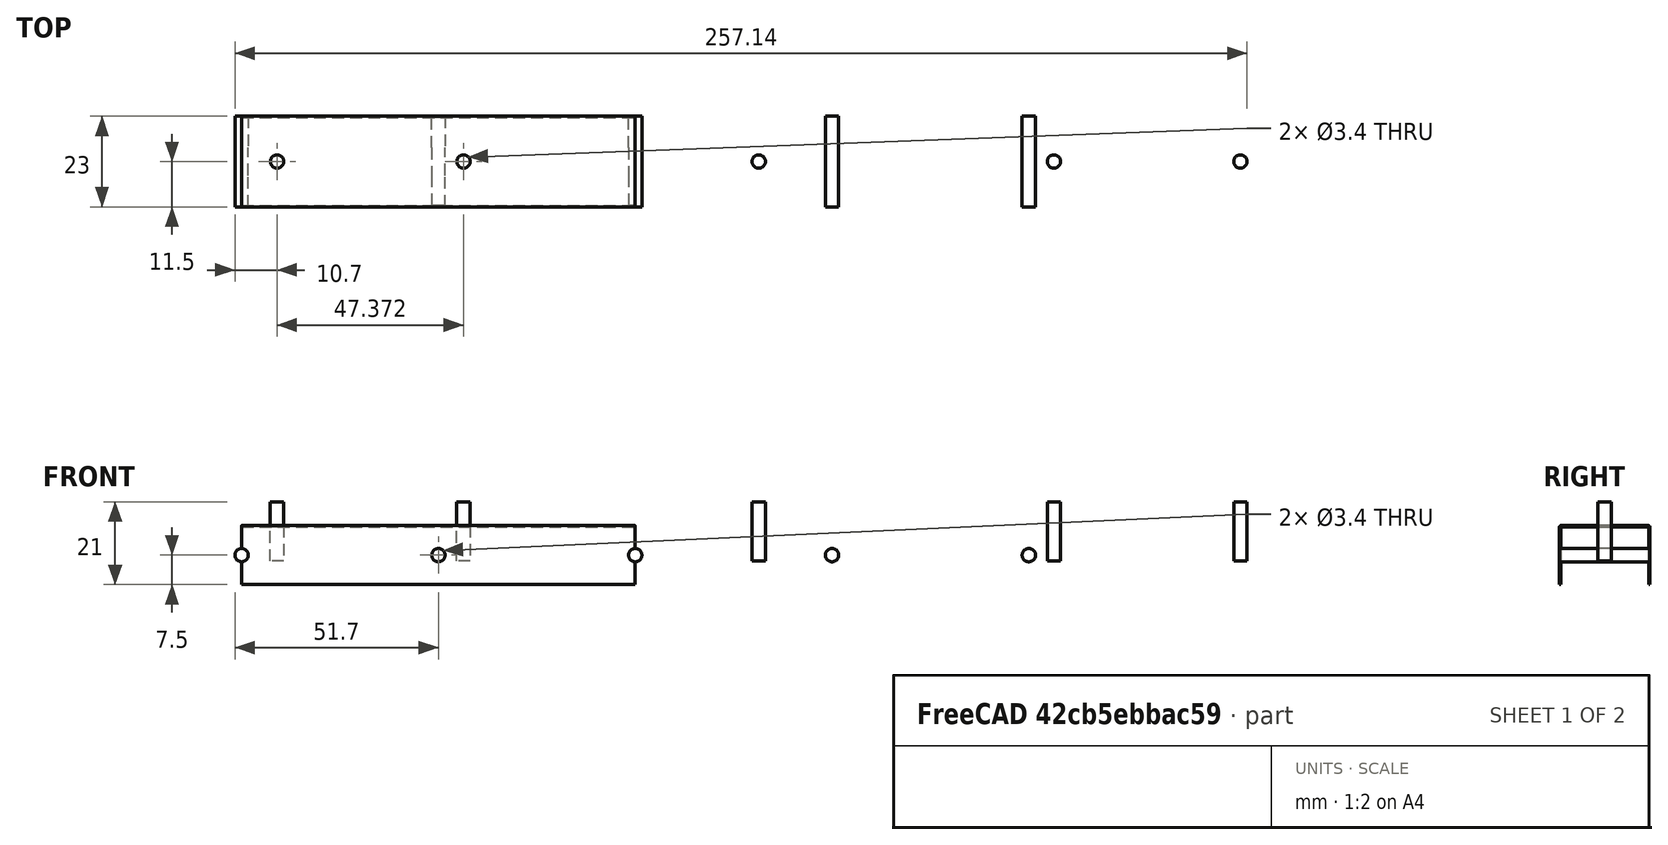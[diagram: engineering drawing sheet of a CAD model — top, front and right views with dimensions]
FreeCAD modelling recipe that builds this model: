
FCSTD DOCUMENT  (FreeCAD 1.1R38827 (Git))
Label: composit_stand3_dropper_fix_fixture_model
License: All rights reserved
LicenseURL: http://en.wikipedia.org/wiki/All_rights_reserved
objects: App::Link×4, Part::FeaturePython×3, PartDesign::SubShapeBinder×2, PartDesign::Body×2, PartDesign::FeaturePython×1, Part::MultiFuse×1, PartDesign::Boolean×1, PartDesign::CoordinateSystem×1
note: 13 computed .brp shape members not serialized (recipe doc carries the construction recipe); baked Part::Feature solids carry a one-line shape summary decoded from their .brp
EXTERNAL_REF file=composit_stand3_dropper_fix_fixture_main.FCStd obj=Sketch
EXTERNAL_REF file=composit_stand3_dropper_fix_fixture_main.FCStd obj=Placment
EXTERNAL_REF file=composit_stand3_main.FCStd obj=Cylinder
EXTERNAL_REF file=composit_stand3_dropper_fix_fixture_main.FCStd obj=Join
EXTERNAL_REF file=composit_stand3_dropper_fix_main.FCStd obj=Join

FEATURE [PartDesign::SubShapeBinder] Binder
  BindCopyOnChange = 0
  BindMode = 0
  ClaimChildren = true
  Fuse = false
  MakeFace = true
  OffsetFill = false
  OffsetIntersection = false
  OffsetJoinType = 0
  OffsetOpenResult = false
  PartialLoad = false
  Placement = pos=(0,0,0) rot=(0.57735,0.57735,0.57735;2.0944rad)
  Relative = false
  Support = -> [<external composit_stand3_dropper_fix_fixture_main.FCStd>#Sketch]
  _Version = 2
  expr: Placement = Support[0][0].Placement
FEATURE [PartDesign::SubShapeBinder] Binder001
  BindCopyOnChange = 0
  BindMode = 0
  ClaimChildren = true
  Context = -> Body [Binder001.]
  Fuse = false
  MakeFace = true
  OffsetFill = false
  OffsetIntersection = false
  OffsetJoinType = 0
  OffsetOpenResult = false
  PartialLoad = false
  Placement = pos=(0,0,0) rot=(0.57735,0.57735,0.57735;2.0944rad)
  Relative = false
  Support = -> [Binder]
  _Version = 2
  expr: Placement = Support[0][0].Placement
FEATURE [PartDesign::FeaturePython] BaseBend  # WARN: FeaturePython — macro-defined, semantics opaque (R4)
  BendSide = 1
  BendSketch = -> Binder001
  MidPlane = false
  Reverse = false
  Suppressed = false
  length = 100
  radius = 0.1
  thickness = 0.3
FEATURE [App::Link] Link  label="Placment"
  LinkTransform = true
  LinkedObject = -> <external composit_stand3_dropper_fix_fixture_main.FCStd>#Placment
FEATURE [App::Link] Link001  label="hole_3.4mm"
  LinkedObject = -> <external composit_stand3_main.FCStd>#Cylinder
FEATURE [App::Link] Link002  label="Join"
  LinkedObject = -> <external composit_stand3_dropper_fix_fixture_main.FCStd>#Join
FEATURE [PartDesign::Body] Body001
  AllowCompound = false
  Origin = -> Origin001
FEATURE [App::Link] Link003  label="fix"
  LinkedObject = -> <external composit_stand3_dropper_fix_main.FCStd>#Join
FEATURE [Part::FeaturePython] Populate001  label="Populate Placment with fix"  # WARN: FeaturePython — macro-defined, semantics opaque (R4)
  Copying = 0
  ExposePlacement = false
  MarkerShape = 1
  MarkerSize = 0
  NumElements = 5
  Object = -> Link003
  OutputCompounding = 0
  PlacementsTo = -> Link
  Referencing = 0
  Type = lattice2PopulateCopies.LatticePopulateCopies
  isLattice = 1
FEATURE [Part::FeaturePython] Join  label="Join001"  # WARN: FeaturePython — macro-defined, semantics opaque (R4)
  ExposePlacement = false
  Interleave = false
  Links = -> [Link002,Populate001]
  MarkerShape = 1
  MarkerSize = 0
  NumElements = 15
  Type = lattice2JoinArrays.JoinArrays
  isLattice = 1
FEATURE [Part::FeaturePython] Populate  label="Populate Join with hole_3.4mm"  # WARN: FeaturePython — macro-defined, semantics opaque (R4)
  Copying = 0
  ExposePlacement = false
  MarkerShape = 1
  MarkerSize = 0
  NumElements = 0
  Object = -> Link001
  OutputCompounding = 1
  PlacementsTo = -> Join
  Referencing = 0
  Type = lattice2PopulateCopies.LatticePopulateCopies
  isLattice = 0
FEATURE [Part::MultiFuse] Fusion
  Shapes = -> [Populate]
FEATURE [PartDesign::Boolean] Boolean
  BaseFeature = -> BaseBend
  Group = -> [Fusion]
  Suppressed = false
  Type = 1
  UsePlacement = true
FEATURE [PartDesign::CoordinateSystem] Local_CS
  AttacherType = Attacher::AttachEngine3D
  AttachmentOffset = pos=(-50,0,0) rot=(0,0,1;0rad)
  AttachmentSupport = -> [XY_Plane]
  MapMode = 5
  Placement = pos=(-50,0,0) rot=(0,0,1;0rad)
  expr: .AttachmentOffset.Base.x = <<Placment>>.LinkedObject.Placement.Base.x
FEATURE [PartDesign::Body] Body  label="dropper_fix_fixture"
  AllowCompound = false
  Group = -> [Binder001,BaseBend,Boolean,Local_CS]
  Origin = -> Origin
  Tip = -> Boolean

RESOLVED EXTERNAL PARTS (link-assembly join: the EXTERNAL_REF files above that resolve inside this repo's crawl, each included once):
---- part composit_stand3_main.FCStd = doc fcstd_90b2f18ea94f ----
FCSTD DOCUMENT  (FreeCAD 1.1R38827 (Git))
Label: composit_stand3_main
License: All rights reserved
LicenseURL: http://en.wikipedia.org/wiki/All_rights_reserved
objects: Part::Cylinder×2, Sketcher::SketchObject×1, Part::FeaturePython×1
note: 5 computed .brp shape members not serialized (recipe doc carries the construction recipe); baked Part::Feature solids carry a one-line shape summary decoded from their .brp

FEATURE [Sketcher::SketchObject] Sketch  label="main_sketch"
  ArcFitTolerance = 0
  FullyConstrained = true
  MakeInternals = false
  sketch-geometry (4):
    g0: LineSegment [constr] StartX=0 StartY=0 StartZ=0 EndX=8.37158 EndY=14.5 EndZ=0
    g1: LineSegment StartX=8.37158 StartY=14.5 StartZ=0 EndX=351.872 EndY=14.5 EndZ=0
    g2: LineSegment StartX=351.872 StartY=14.5 StartZ=0 EndX=351.872 EndY=0 EndZ=0
    g3: GeomPoint [constr] X=351.872 Y=-14.5 Z=0
  constraints (13):
    c: Coincident(g-1,g0)
    c: Horizontal(g1)
    c: Coincident(g1,g2)
    c: PointOnObject(g2,g-1)
    c: Vertical(g2)
    c: Angle(g0) = 1.0472
    c: DistanceX(g0,g1) = 343.5  'face_width'
    c: DistanceY(g3,g1) = 29  'end_width'
    c: Symmetric(g3,g1,g2)
    c: DistanceX(g0) = 8.37158  'x_face_offset'
    c: Coincident(g1,g0)
    c: Distance(g0) = 16.7432  'corner_distance'
    c: DistanceY(g0,g0) = 14.5
FEATURE [Part::FeaturePython] LinearArray  label="modules_placement_x"  # WARN: FeaturePython — macro-defined, semantics opaque (R4)
  Alignment = 0
  CellStart = A1
  Count = 2
  Dir = (1,0,0)
  DirIsDriven = true
  DistributionLaw = 0
  DrivenProperty = 1
  EndInclusive = true
  ExposePlacement = false
  GeneratorMode = 0
  MarkerShape = 1
  MarkerSize = 0
  NumElements = 2
  OrientMode = 1
  Placement = pos=(8.37158,14.5,0) rot=(0,0,1;0rad)
  Point = (0,0,0)
  PointIsDriven = true
  Reverse = false
  SpanEnd = 248
  SpanStart = 98
  Step = 150
  Type = lattice2LinearArray.LinearArray
  VSGVersion = 1
  Values = 98.0 | 248.0
  ValuesSource = 2
  isLattice = 1
  expr: .Placement.Base.x = <<main_sketch>>.Constraints.end_width / 2 / tan(60)
  expr: .Placement.Base.y = <<main_sketch>>.Constraints.end_width / 2
FEATURE [Part::Cylinder] Cylinder  label="hole_3.4mm"
  Angle = 360
  AttacherType = Attacher::AttachEngine3D
  FirstAngle = 0
  Height = 15
  Radius = 1.7
  SecondAngle = 0
FEATURE [Part::Cylinder] Cylinder001  label="hole_3.4mm_rev"
  Angle = 360
  AttacherType = Attacher::AttachEngine3D
  FirstAngle = 0
  Height = 15
  Placement = pos=(0,0,0) rot=(1,0,0;3.14159rad)
  Radius = 1.7
  SecondAngle = 0
